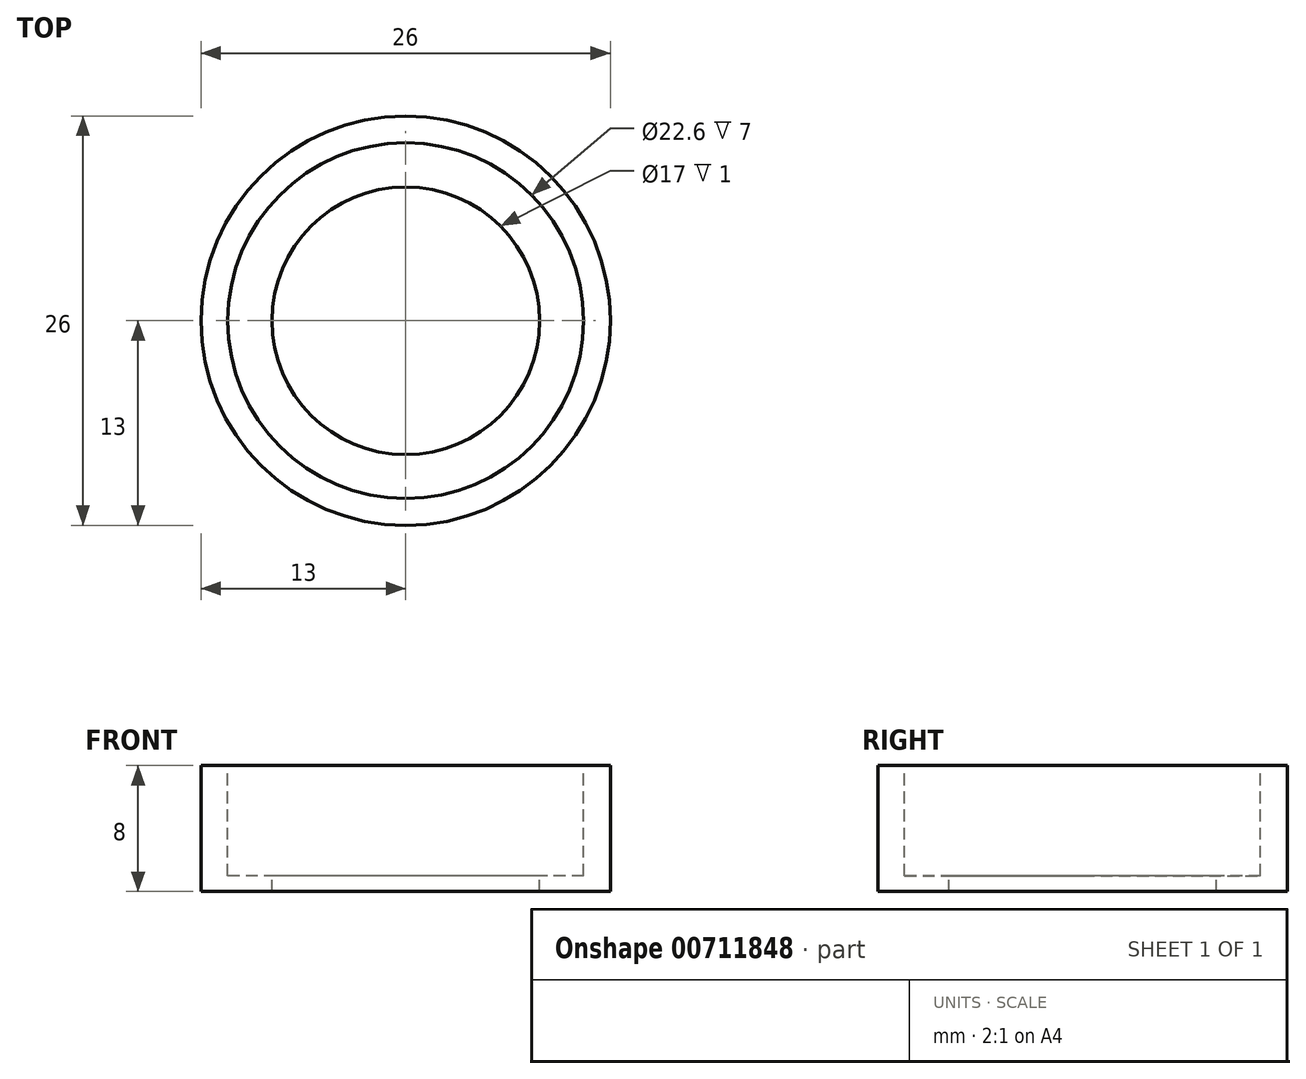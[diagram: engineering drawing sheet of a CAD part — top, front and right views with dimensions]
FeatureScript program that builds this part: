
annotation { "Feature Type Name" : "Feature", "Feature Type Description" : "" }
export const myFeature = defineFeature(function(context is Context, id is Id, definition is map)
    precondition{}
    {
        {
            var Q0;
            Q0=qCreatedBy(makeId("Top.planeOp"),FACE);
            var sketch = newSketch(context, id + "F0", { "sketchPlane" : qUnion([Q0])});
            skCircle(sketch, "E0", {"center": v(0, 0) * mm, "radius": 13 * mm});
            skSolve(sketch);
        }
        {
            var Q0;
            Q0=qSketchRegion(id+"F0",true);
            extrude(context, id + "F1", {"entities" : qUnion([Q0]), "depth" : 8 * mm, "offsetDistance" : 25 * mm});
        }
        {
            var Q0;
            Q0=makeQuery(id+"F1.opExtrude","CAP_FACE",FACE,{"disambiguationData":[OSD([sQuery(id+"F0.wireOp",EDGE,"E0")])],"isStart":false});
            var sketch = newSketch(context, id + "F2", { "sketchPlane" : qUnion([Q0])});
            skCircle(sketch, "E1", {"center": v(0, 0) * mm, "radius": 11.3 * mm});
            skSolve(sketch);
        }
        {
            var Q0;
            Q0=makeQuery(id+"F2.imprint","IMPRINT",FACE,{"disambiguationData":[TD([[makeQuery(id+"F2.imprint","IMPRINT",EDGE,{"derivedFrom":sQuery(id+"F2.wireOp",EDGE,"E1")}),1.0]])]});
            extrude(context, id + "F3", {"entities" : qUnion([Q0]), "operationType" : NewBodyOperationType.REMOVE, "oppositeDirection" : true, "depth" : 7 * mm, "offsetDistance" : 25 * mm});
        }
        {
            var Q0;
            Q0=makeQuery(id+"F3.boolean.opBoolean","COPY",FACE,{"derivedFrom":makeQuery(id+"F3.opExtrude","CAP_FACE",FACE,{"disambiguationData":[OSD([sQuery(id+"F2.wireOp",EDGE,"E1")])],"isStart":false})});
            var sketch = newSketch(context, id + "F4", { "sketchPlane" : qUnion([Q0])});
            skCircle(sketch, "E2", {"center": v(0, 0) * mm, "radius": 8.5 * mm});
            skSolve(sketch);
        }
        {
            var Q0;
            Q0=makeQuery(id+"F4.imprint","IMPRINT",FACE,{"disambiguationData":[TD([[makeQuery(id+"F4.imprint","IMPRINT",EDGE,{"derivedFrom":sQuery(id+"F4.wireOp",EDGE,"E2")}),1.0]])]});
            extrude(context, id + "F5", {"entities" : qUnion([Q0]), "operationType" : NewBodyOperationType.REMOVE, "oppositeDirection" : true, "depth" : 1 * mm, "offsetDistance" : 25 * mm});
        }
    });
